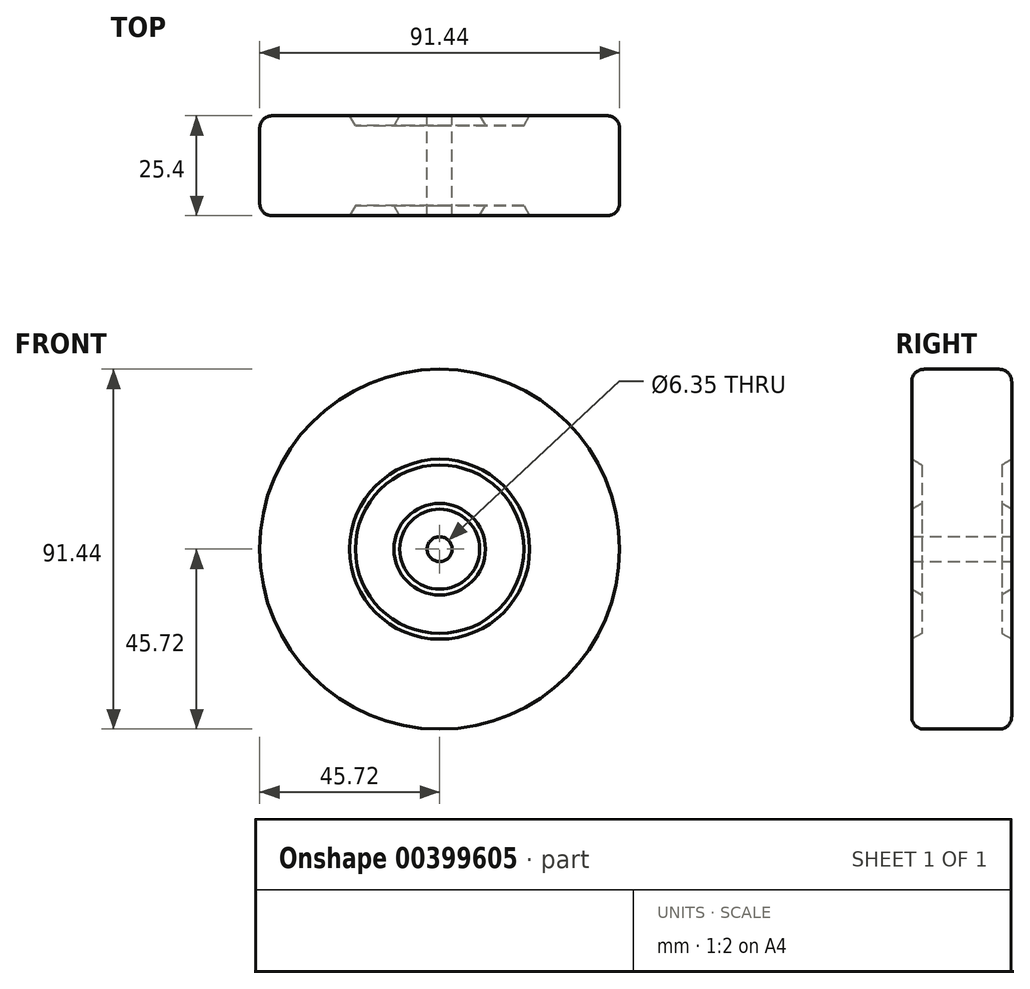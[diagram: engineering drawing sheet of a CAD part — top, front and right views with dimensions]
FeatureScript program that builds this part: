
annotation { "Feature Type Name" : "Feature", "Feature Type Description" : "" }
export const myFeature = defineFeature(function(context is Context, id is Id, definition is map)
    precondition{}
    {
        {
            var Q0;
            Q0=qCreatedBy(makeId("Right.planeOp"),FACE);
            var sketch = newSketch(context, id + "F0", { "sketchPlane" : qUnion([Q0])});
            skLineSegment(sketch, "E0", {"start": v(0, 0) * mm, "end": v(45.88, 0) * mm, "construction": true});
            skLineSegment(sketch, "E1", {"start": v(12.7, 3.18) * mm, "end": v(12.7, 10.16) * mm});
            skLineSegment(sketch, "E2", {"start": v(12.7, 10.16) * mm, "end": v(10.16, 11.63) * mm});
            skLineSegment(sketch, "E3", {"start": v(10.16, 11.63) * mm, "end": v(10.16, 21.4) * mm});
            skLineSegment(sketch, "E4", {"start": v(10.16, 21.4) * mm, "end": v(12.7, 22.86) * mm});
            skLineSegment(sketch, "E5", {"start": v(12.7, 22.86) * mm, "end": v(12.7, 42.55) * mm});
            skLineSegment(sketch, "E6.MirrorCS", {"start": v(-10.16, 21.4) * mm, "end": v(-12.7, 22.86) * mm});
            skLineSegment(sketch, "E7.MirrorCS", {"start": v(-12.7, 10.16) * mm, "end": v(-10.16, 11.63) * mm});
            skLineSegment(sketch, "E8.MirrorCS", {"start": v(-10.16, 11.63) * mm, "end": v(-10.16, 21.4) * mm});
            skLineSegment(sketch, "E9.MirrorCS", {"start": v(0, 0) * mm, "end": v(-45.88, 0) * mm, "construction": true});
            skLineSegment(sketch, "E10.MirrorCS", {"start": v(-12.7, 3.18) * mm, "end": v(-12.7, 10.16) * mm});
            skLineSegment(sketch, "E11.MirrorCS", {"start": v(-12.7, 22.86) * mm, "end": v(-12.7, 42.55) * mm});
            skLineSegment(sketch, "E12", {"start": v(-9.52, 45.72) * mm, "end": v(9.52, 45.72) * mm});
            skPoint(sketch, "E13.visualSharp", {"position": v(-12.7, 45.72) * mm});
            skArc(sketch, "E13.filletArc", {"start": v(-9.52, 45.72) * mm, "mid": v(-11.77, 44.8) * mm, "end": v(-12.7, 42.55) * mm});
            skPoint(sketch, "E14.visualSharp", {"position": v(12.7, 45.72) * mm});
            skArc(sketch, "E14.filletArc", {"start": v(12.7, 42.55) * mm, "mid": v(11.77, 44.8) * mm, "end": v(9.52, 45.72) * mm});
            skLineSegment(sketch, "E15", {"start": v(-12.7, 3.18) * mm, "end": v(12.7, 3.18) * mm});
            skSolve(sketch);
        }
        {
            var Q0;
            Q0=makeQuery(id+"F0.imprint","IMPRINT",FACE,{"disambiguationData":[TD([[makeQuery(id+"F0.imprint","IMPRINT",EDGE,{"derivedFrom":sQuery(id+"F0.wireOp",EDGE,"E1")}),1.0]])]});
            var Q1;
            Q1=sQuery(id+"F0.wireOp",EDGE,"E9.MirrorCS");
            revolve(context, id + "F1", {"entities" : qUnion([Q0]), "axis" : qUnion([Q1]), "revolveType" : RevolveType.FULL});
        }
        {
            var Q0;
            Q0=makeQuery(id+"F1.opRevolve","SWEPT_BODY",BODY,{"disambiguationData":[OSD([sQuery(id+"F0.wireOp",EDGE,"E1"),sQuery(id+"F0.wireOp",EDGE,"E2"),sQuery(id+"F0.wireOp",EDGE,"E3"),sQuery(id+"F0.wireOp",EDGE,"E4"),sQuery(id+"F0.wireOp",EDGE,"E5"),sQuery(id+"F0.wireOp",EDGE,"E6.MirrorCS"),sQuery(id+"F0.wireOp",EDGE,"E7.MirrorCS"),sQuery(id+"F0.wireOp",EDGE,"E8.MirrorCS"),sQuery(id+"F0.wireOp",EDGE,"E10.MirrorCS"),sQuery(id+"F0.wireOp",EDGE,"E11.MirrorCS"),sQuery(id+"F0.wireOp",EDGE,"E12"),sQuery(id+"F0.wireOp",EDGE,"E13.filletArc"),sQuery(id+"F0.wireOp",EDGE,"E14.filletArc"),sQuery(id+"F0.wireOp",EDGE,"E15")])]});
            transform(context, id + "F2", {"entities" : qUnion([Q0]), "transformType" : TransformType.TRANSLATION_3D, "dx" : 0 * mm, "dy" : 0 * mm, "dz" : 0 * mm, "makeCopy" : true});
        }
        {
            var Q0;
            Q0=makeQuery(id+"F1.opRevolve","SWEPT_BODY",BODY,{"disambiguationData":[OSD([sQuery(id+"F0.wireOp",EDGE,"E1"),sQuery(id+"F0.wireOp",EDGE,"E2"),sQuery(id+"F0.wireOp",EDGE,"E3"),sQuery(id+"F0.wireOp",EDGE,"E4"),sQuery(id+"F0.wireOp",EDGE,"E5"),sQuery(id+"F0.wireOp",EDGE,"E6.MirrorCS"),sQuery(id+"F0.wireOp",EDGE,"E7.MirrorCS"),sQuery(id+"F0.wireOp",EDGE,"E8.MirrorCS"),sQuery(id+"F0.wireOp",EDGE,"E10.MirrorCS"),sQuery(id+"F0.wireOp",EDGE,"E11.MirrorCS"),sQuery(id+"F0.wireOp",EDGE,"E12"),sQuery(id+"F0.wireOp",EDGE,"E13.filletArc"),sQuery(id+"F0.wireOp",EDGE,"E14.filletArc"),sQuery(id+"F0.wireOp",EDGE,"E15")])]});
            deleteBodies(context, id + "F3", {"entities" : qUnion([Q0])});
        }
    });
